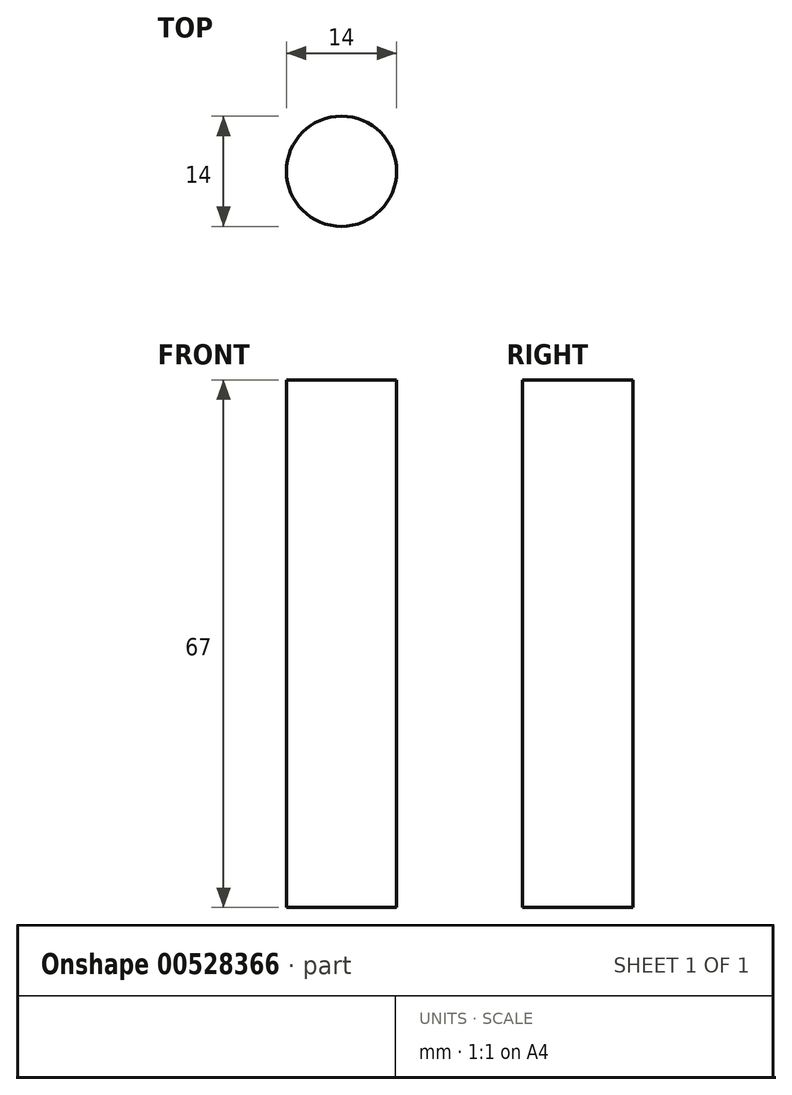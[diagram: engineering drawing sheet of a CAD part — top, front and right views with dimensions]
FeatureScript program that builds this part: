
annotation { "Feature Type Name" : "Feature", "Feature Type Description" : "" }
export const myFeature = defineFeature(function(context is Context, id is Id, definition is map)
    precondition{}
    {
        {
            var Q0;
            Q0=qCreatedBy(makeId("Front.planeOp"),FACE);
            var sketch = newSketch(context, id + "F0", { "sketchPlane" : qUnion([Q0])});
            skLineSegment(sketch, "E0", {"start": v(0, 0) * mm, "end": v(0, 42.24) * mm});
            skLineSegment(sketch, "E1", {"start": v(0, 42.24) * mm, "end": v(7, 42.24) * mm});
            skLineSegment(sketch, "E2", {"start": v(7, 42.24) * mm, "end": v(7, -24.76) * mm});
            skLineSegment(sketch, "E3", {"start": v(7, -24.76) * mm, "end": v(0, -24.76) * mm});
            skLineSegment(sketch, "E4", {"start": v(0, -24.76) * mm, "end": v(0, 0) * mm});
            skSolve(sketch);
        }
        {
            var Q0;
            Q0=makeQuery(id+"F0.imprint","IMPRINT",FACE,{"disambiguationData":[TD([[makeQuery(id+"F0.imprint","IMPRINT",EDGE,{"derivedFrom":sQuery(id+"F0.wireOp",EDGE,"E0")}),-1.0]])]});
            var Q1;
            Q1=sQuery(id+"F0.wireOp",EDGE,"E0");
            revolve(context, id + "F1", {"entities" : qUnion([Q0]), "axis" : qUnion([Q1]), "revolveType" : RevolveType.FULL});
        }
    });
